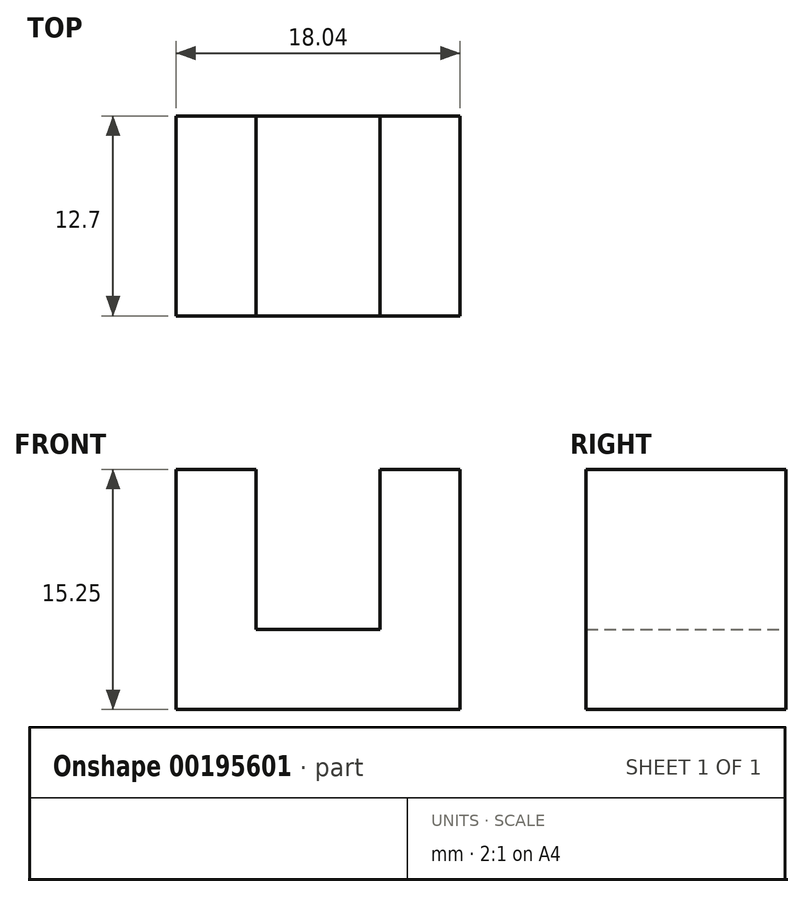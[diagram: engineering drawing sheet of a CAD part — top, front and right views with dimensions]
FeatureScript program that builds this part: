
annotation { "Feature Type Name" : "Feature", "Feature Type Description" : "" }
export const myFeature = defineFeature(function(context is Context, id is Id, definition is map)
    precondition{}
    {
        {
            var Q0;
            Q0=qCreatedBy(makeId("Front.planeOp"),FACE);
            var sketch = newSketch(context, id + "F0", { "sketchPlane" : qUnion([Q0])});
            skLineSegment(sketch, "E0.bottom", {"start": v(-49.45, 17.52) * mm, "end": v(-31.41, 17.52) * mm});
            skLineSegment(sketch, "E0.top", {"start": v(-44.37, 22.6) * mm, "end": v(-36.5, 22.6) * mm});
            skLineSegment(sketch, "E0.left", {"start": v(-49.45, 17.52) * mm, "end": v(-49.45, 22.6) * mm});
            skLineSegment(sketch, "E0.right", {"start": v(-31.41, 17.52) * mm, "end": v(-31.41, 22.6) * mm});
            skLineSegment(sketch, "E1.top", {"start": v(-49.45, 32.76) * mm, "end": v(-44.37, 32.76) * mm});
            skLineSegment(sketch, "E1.left", {"start": v(-49.45, 22.6) * mm, "end": v(-49.45, 32.76) * mm});
            skLineSegment(sketch, "E1.right", {"start": v(-44.37, 22.6) * mm, "end": v(-44.37, 32.76) * mm});
            skLineSegment(sketch, "E2.top", {"start": v(-31.41, 32.77) * mm, "end": v(-36.5, 32.77) * mm});
            skLineSegment(sketch, "E2.left", {"start": v(-31.41, 22.6) * mm, "end": v(-31.41, 32.77) * mm});
            skLineSegment(sketch, "E2.right", {"start": v(-36.5, 22.6) * mm, "end": v(-36.5, 32.77) * mm});
            skPoint(sketch, "E3", {"position": v(-44.37, 22.6) * mm});
            skPoint(sketch, "E4", {"position": v(-36.5, 22.6) * mm});
            skSolve(sketch);
        }
        {
            var Q0;
            Q0 = qSketchRegion(id + "F0", true);
            extrude(context, id + "F1", {"entities" : qUnion([Q0]), "depth" : 12.7 * mm});
        }
    });
